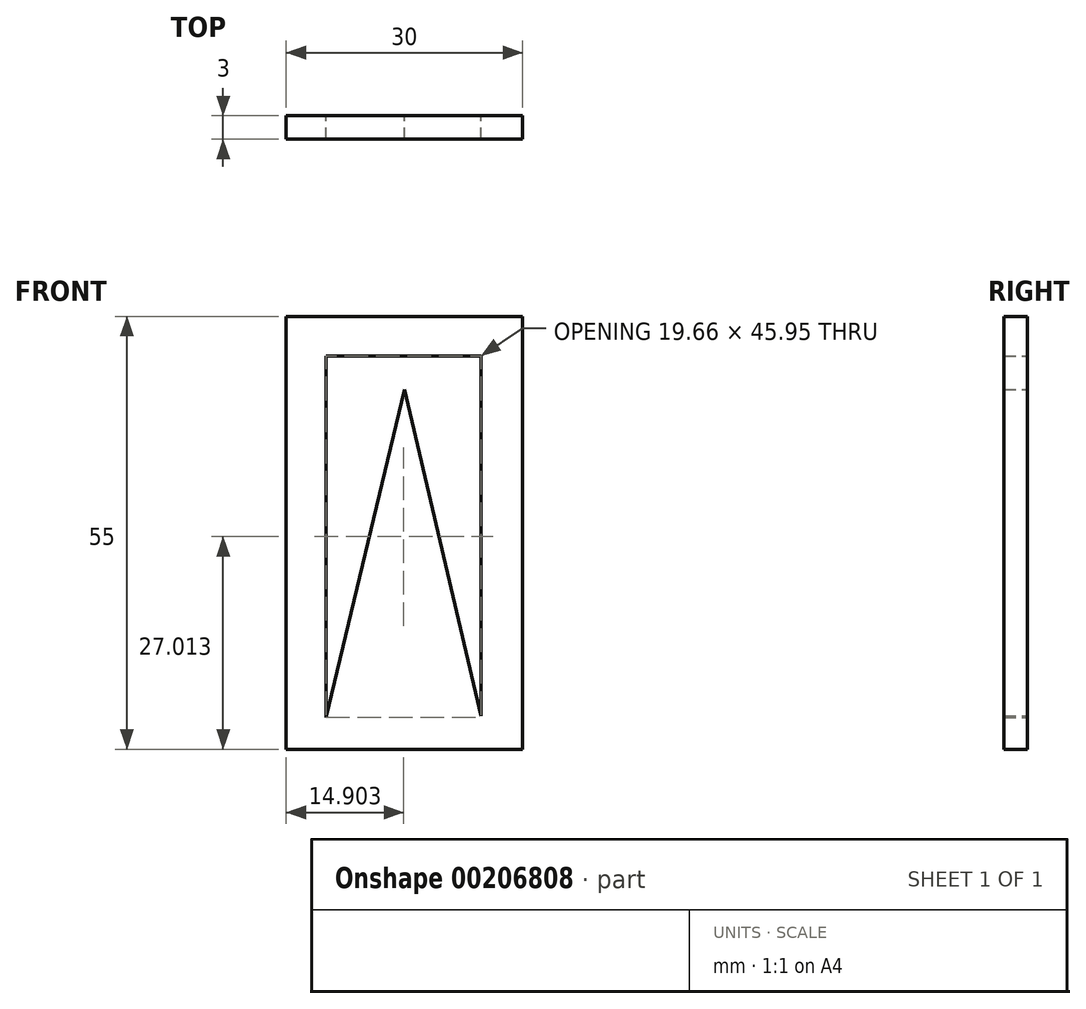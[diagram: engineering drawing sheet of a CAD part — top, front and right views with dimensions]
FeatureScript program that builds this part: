
annotation { "Feature Type Name" : "Feature", "Feature Type Description" : "" }
export const myFeature = defineFeature(function(context is Context, id is Id, definition is map)
    precondition{}
    {
        {
            var Q0;
            Q0=qCreatedBy(makeId("Front.planeOp"),FACE);
            var sketch = newSketch(context, id + "F0", { "sketchPlane" : qUnion([Q0])});
            skLineSegment(sketch, "E0.bottom", {"start": v(15, -27.5) * mm, "end": v(-15, -27.5) * mm});
            skLineSegment(sketch, "E0.top", {"start": v(15, 27.5) * mm, "end": v(-15, 27.5) * mm});
            skLineSegment(sketch, "E0.left", {"start": v(15, -27.5) * mm, "end": v(15, 27.5) * mm});
            skLineSegment(sketch, "E0.right", {"start": v(-15, -27.5) * mm, "end": v(-15, 27.5) * mm});
            skPoint(sketch, "E0.middle", {"position": v(0, 0) * mm});
            skLineSegment(sketch, "E1", {"start": v(-9.93, 22.49) * mm, "end": v(-9.93, -23.46) * mm});
            skLineSegment(sketch, "E2", {"start": v(-9.93, -23.46) * mm, "end": v(0, 18.2) * mm});
            skLineSegment(sketch, "E3", {"start": v(0, 18.2) * mm, "end": v(9.73, -23.26) * mm});
            skLineSegment(sketch, "E4", {"start": v(9.73, -23.26) * mm, "end": v(9.73, 22.49) * mm});
            skLineSegment(sketch, "E5", {"start": v(9.73, 22.49) * mm, "end": v(-9.93, 22.49) * mm});
            skSolve(sketch);
        }
        {
            var Q0;
            Q0=makeQuery(id+"F0.imprint","IMPRINT",FACE,{"disambiguationData":[TD([[makeQuery(id+"F0.imprint","IMPRINT",EDGE,{"derivedFrom":sQuery(id+"F0.wireOp",EDGE,"E0.bottom")}),-1.0]])]});
            extrude(context, id + "F1", {"entities" : qUnion([Q0]), "depth" : 3 * mm});
        }
    });
